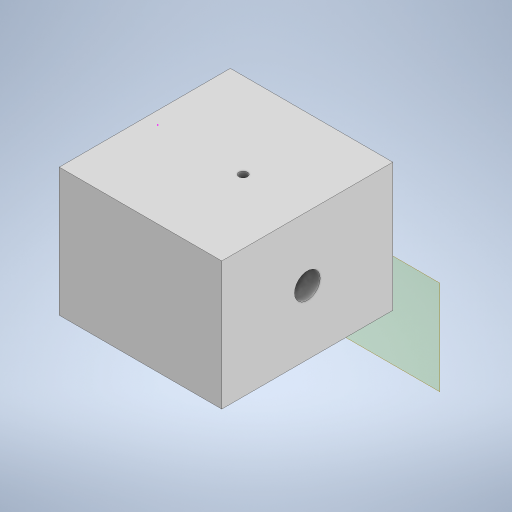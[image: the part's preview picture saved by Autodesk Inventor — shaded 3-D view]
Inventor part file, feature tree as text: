
AUTODESK INVENTOR PART (.ipt)
format: ipt  version: 2023 (Build 270158000, 158)  size: 288,768 bytes
history: native  units: mm
features: sketch x9, extrude x7, plane x6
ambient origin geometry x8: Origin, YZ Plane, XZ Plane, XY Plane, X Axis, Y Axis, Z Axis, Center Point
bodies: Body1 (feature_tree)
feature tree (22):
  plane  "Work Plane13"
  extrude  "Extrusion34"  Depth=40.0mm
  sketch  "Sketch46"  dims[d144=30.0mm d145=0.0mm d146=36.0mm]
  plane  "Work Plane11"
  extrude  "Extrusion35"  Depth=36.0mm
  sketch  "Sketch48"  dims[d150=0.0mm d151=0.0mm d156=20.0mm]
  extrude  "Extrusion36"  Depth=2.0mm
  plane  "Work Plane7"
  extrude  "Extrusion38"  Depth=20.0mm
  plane  "Work Plane4"
  extrude  "Extrusion39"  Depth=15.0mm TaperAngle=0.0deg
  plane  "Work Plane1"
  plane  "Work Plane6"
  extrude  "Extrusion42"  Depth=20.0mm
  extrude  "Extrusion44"  Depth=6.0mm
  sketch  "Sketch45"  dims[d142=38.0mm d143=40.0mm]
  sketch  "Sketch47"  dims[d147=30.0mm d148=-2.617994mm d149=2.0mm]
  sketch  "Sketch49"  dims[d157=15.0mm d158=15.0mm d159=0.0mm]
  sketch  "Sketch58"  dims[d160=4.0mm d161=20.0mm]
  sketch  "Sketch59"  dims[d162=35.0mm d163=0.0mm d172=6.0mm]
  sketch  "Sketch62"  dims[d173=0.0mm d174=0.0mm]
  sketch  "Sketch65"  dims[d177=5.0mm d178=0.0mm d49=0.5mm d50=0.872665mm d51=0.5mm d52=0.872665mm d130=0.5mm d131=0.872665mm d132=0.5mm d133=0.872665mm]
